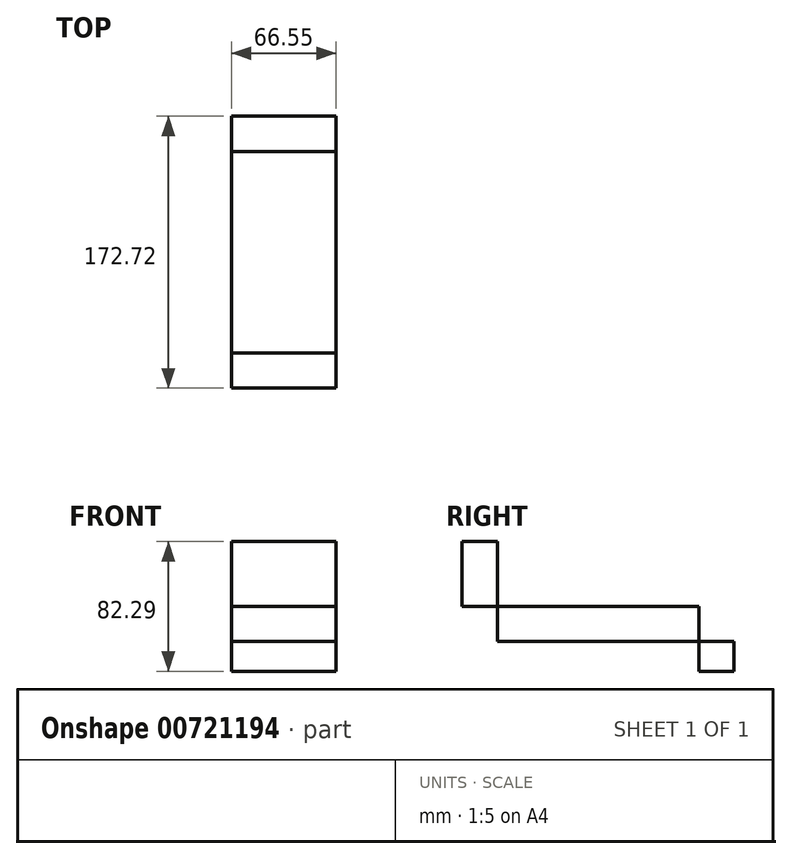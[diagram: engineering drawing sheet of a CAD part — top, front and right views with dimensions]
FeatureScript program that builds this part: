
annotation { "Feature Type Name" : "Feature", "Feature Type Description" : "" }
export const myFeature = defineFeature(function(context is Context, id is Id, definition is map)
    precondition{}
    {
        {
            var Q0;
            Q0=qCreatedBy(makeId("Right.planeOp"),FACE);
            var sketch = newSketch(context, id + "F0", { "sketchPlane" : qUnion([Q0])});
            skLineSegment(sketch, "E0.bottom", {"start": v(86.36, -11.18) * mm, "end": v(-86.36, -11.18) * mm});
            skLineSegment(sketch, "E0.top", {"start": v(86.36, 11.18) * mm, "end": v(-86.36, 11.18) * mm});
            skLineSegment(sketch, "E0.left", {"start": v(86.36, -11.18) * mm, "end": v(86.36, 11.18) * mm});
            skLineSegment(sketch, "E0.right", {"start": v(-86.36, -11.18) * mm, "end": v(-86.36, 11.18) * mm});
            skPoint(sketch, "E0.middle", {"position": v(0, 0) * mm});
            skLineSegment(sketch, "E1.bottom", {"start": v(-86.36, -11.18) * mm, "end": v(-64, -11.18) * mm});
            skLineSegment(sketch, "E1.top", {"start": v(-86.36, 52.32) * mm, "end": v(-64, 52.32) * mm});
            skLineSegment(sketch, "E1.left", {"start": v(-86.36, -11.18) * mm, "end": v(-86.36, 52.32) * mm});
            skLineSegment(sketch, "E1.right", {"start": v(-64, -11.18) * mm, "end": v(-64, 52.32) * mm});
            skLineSegment(sketch, "E2.bottom", {"start": v(86.36, 11.18) * mm, "end": v(64, 11.18) * mm});
            skLineSegment(sketch, "E2.top", {"start": v(86.36, -29.97) * mm, "end": v(64, -29.97) * mm});
            skLineSegment(sketch, "E2.left", {"start": v(86.36, 11.18) * mm, "end": v(86.36, -29.97) * mm});
            skLineSegment(sketch, "E2.right", {"start": v(64, 11.18) * mm, "end": v(64, -29.97) * mm});
            skSolve(sketch);
        }
        {
            var Q0;
            {var subQ5=sQuery(id+"F0.wireOp",EDGE,"E1.top");Q0=makeQuery(id+"F0.imprint","IMPRINT",FACE,{"disambiguationData":[TD([[makeQuery(id+"F0.imprint","IMPRINT",EDGE,{"derivedFrom":subQ5}),-1.0]])]});}
            var Q1;
            {var subQ5=sQuery(id+"F0.wireOp",EDGE,"E1.bottom");Q1=makeQuery(id+"F0.imprint","IMPRINT",FACE,{"disambiguationData":[TD([[makeQuery(id+"F0.imprint","IMPRINT",EDGE,{"derivedFrom":subQ5}),1.0]])]});}
            var Q2;
            {var subQ1=sQuery(id+"F0.wireOp",EDGE,"E0.bottom");var subQ3=sQuery(id+"F0.wireOp",EDGE,"E2.right");var subQ4=makeQuery(id+"F0.imprint","INTERSECT",VERTEX,{"derivedFrom":[subQ1,subQ3]});Q2=makeQuery(id+"F0.imprint","IMPRINT",FACE,{"disambiguationData":[TD([[makeQuery(id+"F0.imprint","IMPRINT",EDGE,{"disambiguationData":[TD([[subQ4,-1.0]])],"derivedFrom":subQ1}),-1.0]])]});}
            var Q3;
            {var subQ5=sQuery(id+"F0.wireOp",EDGE,"E2.bottom");Q3=makeQuery(id+"F0.imprint","IMPRINT",FACE,{"disambiguationData":[TD([[makeQuery(id+"F0.imprint","IMPRINT",EDGE,{"derivedFrom":subQ5}),1.0]])]});}
            var Q4;
            {var subQ5=sQuery(id+"F0.wireOp",EDGE,"E2.top");Q4=makeQuery(id+"F0.imprint","IMPRINT",FACE,{"disambiguationData":[TD([[makeQuery(id+"F0.imprint","IMPRINT",EDGE,{"derivedFrom":subQ5}),-1.0]])]});}
            extrude(context, id + "F1", {"entities" : qUnion([Q0, Q1, Q2, Q3, Q4]), "depth" : 66.55 * mm, "offsetDistance" : 25.4 * mm});
        }
    });
